# Revit family: Electronics_Commercial-Audio_Biamp_Local-Input-Panel_ALINP
name_source: partatom
category: Communication Devices
units: mm (PartAtom-declared; Revit-internal decimal feet)

## family parameters
Cut with Voids When Loaded = No
Host = Face
Maintain Annotation Orientation = No
OmniClass Number = 23.85.10.11.14
OmniClass Title = Audio Equipment
Part Type = Normal
Room Calculation Point = No
Round Connector Dimension = Use Diameter
Shared = No

## types (1)
- ALINP
    Active = yes
    Apparent Load = 0 VA
    Connector Description = Euroblock 3-pole
    Cut-out dimensions in mm = 51 x 51
    Default Elevation = 4' - 0"
    Depth = 0' - 2"
    Description = ALINP Active Local Input Panel
    Frequency range = MIC: 150Hz - 20kHz / Line: 50Hz - 20kHz
    Height = 0' - 3 1/2"
    Housing Material = Biamp - Plastic - White
    Input impedance Ohm = MIC: 4k / Line: 8.5k
    Inputs = balanced mic & unbalanced line
    Manufacturer = Biamp
    Max Power Consumption = 0 W
    Max. cable length in m = 600
    Model = ALINP
    Nominal output level = 1V balanced
    Number of Poles = 1
    Power Factor = 1
    Power type = phantom
    Product Documentation Link = https://downloads.biamp.com
    Product Page URL = https://www.biamp.com
    Product data url = https://www.bimobject.com
    Recommended cable type = 2-core shielded microphone cable
    Sensitivity = unbalanced line: 370mV / balanced mic: 16mV
    Signal to noise level SNR = > 86dB
    Steps = linear
    Stereo/mono = mono
    Total harmonic distortion = < 0.05%
    URL = https://www.biamp.com
    Voltage = 0 V
    Weight = 0.24 lb
    Width = 0' - 3 1/2"

## geometry (parser evidence)
native form markers: Sweep x2
no freeform markers — native parametric forms only
